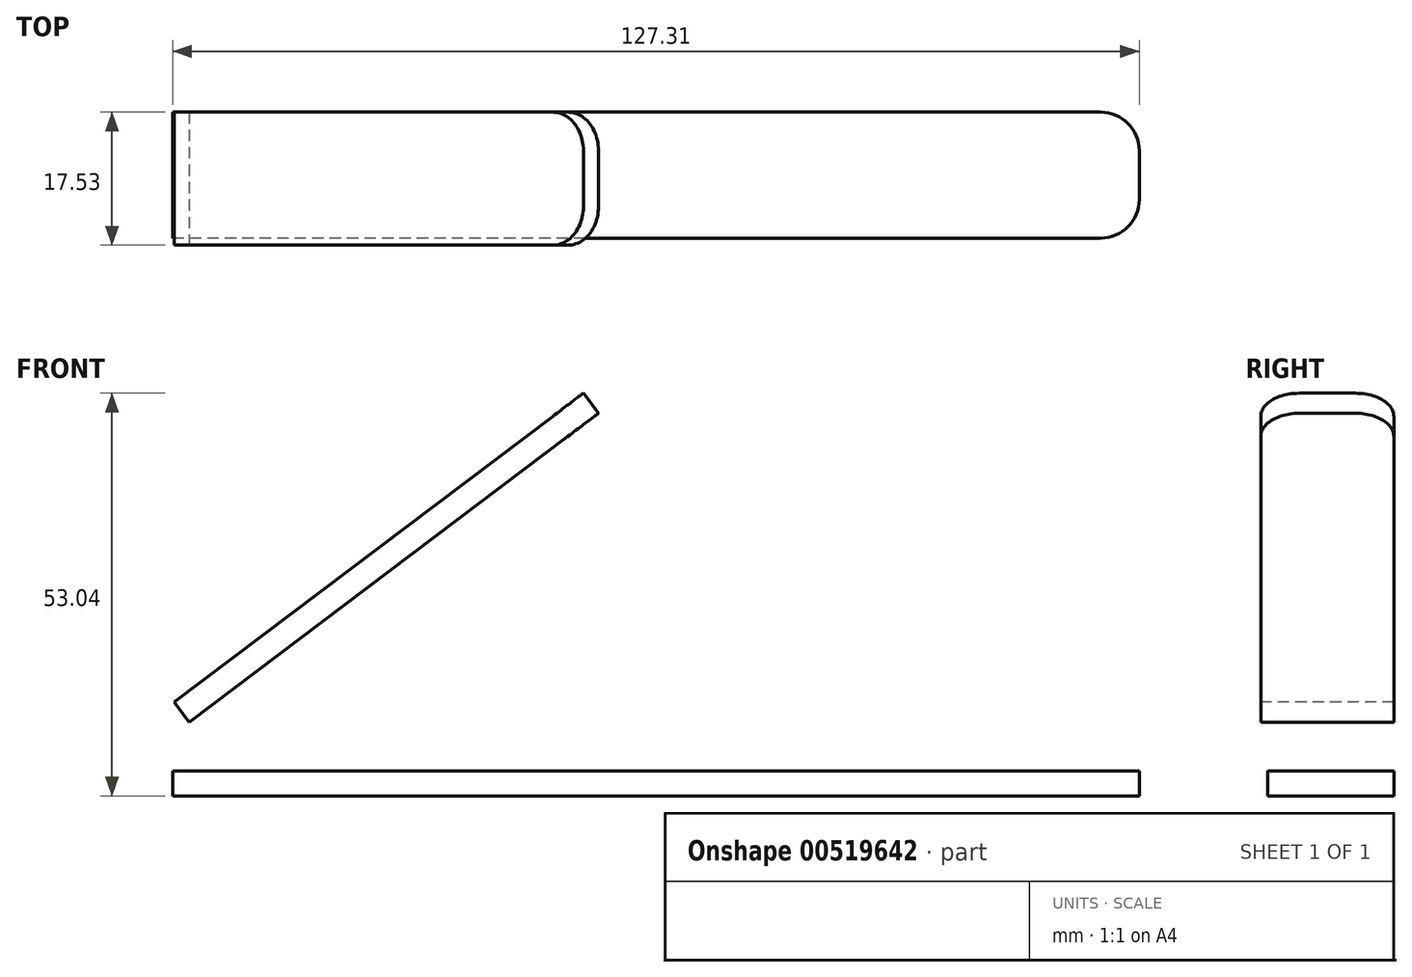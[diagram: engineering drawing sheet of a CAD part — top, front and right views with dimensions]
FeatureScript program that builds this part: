
annotation { "Feature Type Name" : "Feature", "Feature Type Description" : "" }
export const myFeature = defineFeature(function(context is Context, id is Id, definition is map)
    precondition{}
    {
        {
            var Q0;
            Q0=qCreatedBy(makeId("Front.planeOp"),FACE);
            var sketch = newSketch(context, id + "F0", { "sketchPlane" : qUnion([Q0])});
            skLineSegment(sketch, "E0", {"start": v(0, 0) * mm, "end": v(127, 0) * mm});
            skLineSegment(sketch, "E1", {"start": v(0, 12.2) * mm, "end": v(50.68, 50.46) * mm});
            skArc(sketch, "E2", {"start": v(0, 12.2) * mm, "mid": v(-3.04, 6.1) * mm, "end": v(0, 0) * mm});
            skSolve(sketch);
        }
        {
            var Q0;
            Q0=sQuery(id+"F0.wireOp",EDGE,"E1");
            cPlane(context, id + "F1", {"entities" : qUnion([Q0]), "cplaneType" : CPlaneType.LINE_ANGLE, "offset" : 25.4 * mm, "angle" : 90 * degree, "width" : 152.4 * mm, "height" : 152.4 * mm});
        }
        {
            var Q0;
            Q0=qCreatedBy(id+"F1.planeOp",FACE);
            var sketch = newSketch(context, id + "F2", { "sketchPlane" : qUnion([Q0])});
            skLineSegment(sketch, "E3.bottom", {"start": v(75.14, 0) * mm, "end": v(7.6, 0) * mm});
            skLineSegment(sketch, "E3.top", {"start": v(75.14, -17.53) * mm, "end": v(7.6, -17.53) * mm});
            skLineSegment(sketch, "E3.left", {"start": v(75.14, 0) * mm, "end": v(75.14, -17.53) * mm});
            skLineSegment(sketch, "E3.right", {"start": v(7.6, 0) * mm, "end": v(7.6, -17.53) * mm});
            skSolve(sketch);
        }
        {
            var Q0;
            Q0=qCreatedBy(makeId("Top.planeOp"),FACE);
            var sketch = newSketch(context, id + "F3", { "sketchPlane" : qUnion([Q0])});
            skLineSegment(sketch, "E4.bottom", {"start": v(127.31, 0) * mm, "end": v(0, 0) * mm});
            skLineSegment(sketch, "E4.top", {"start": v(127.31, -16.6) * mm, "end": v(0, -16.6) * mm});
            skLineSegment(sketch, "E4.left", {"start": v(127.31, 0) * mm, "end": v(127.31, -16.6) * mm});
            skLineSegment(sketch, "E4.right", {"start": v(0, 0.93) * mm, "end": v(0, -16.6) * mm});
            skSolve(sketch);
        }
        {
            var Q0;
            Q0=qCreatedBy(makeId("Front.planeOp"),FACE);
            cPlane(context, id + "F4", {"entities" : qUnion([Q0]), "cplaneType" : CPlaneType.OFFSET, "offset" : 17.53 * mm, "width" : 152.4 * mm, "height" : 152.4 * mm});
        }
        {
            var Q0;
            {var subQ0=sQuery(id+"F3.wireOp",EDGE,"E4.bottom");Q0=makeQuery(id+"F3.imprint","IMPRINT",FACE,{"disambiguationData":[TD([[makeQuery(id+"F3.imprint","IMPRINT",EDGE,{"derivedFrom":subQ0}),1.0]])]});}
            extrude(context, id + "F5", {"entities" : qUnion([Q0]), "depth" : 3.3 * mm, "offsetDistance" : 25.4 * mm});
        }
        {
            var Q0;
            Q0=makeQuery(id+"F2.imprint","IMPRINT",FACE,{"disambiguationData":[TD([[makeQuery(id+"F2.imprint","IMPRINT",EDGE,{"derivedFrom":sQuery(id+"F2.wireOp",EDGE,"E3.bottom")}),1.0]])]});
            extrude(context, id + "F6", {"entities" : qUnion([Q0]), "oppositeDirection" : true, "depth" : 3.3 * mm, "offsetDistance" : 25.4 * mm});
        }
        {
            var Q0;
            Q0=makeQuery(id+"F6.opExtrude","SWEPT_EDGE",EDGE,{"disambiguationData":[OSD([sQuery(id+"F2.wireOp",EDGE,"E3.bottom"),sQuery(id+"F2.wireOp",EDGE,"E3.left")])]});
            var Q1;
            Q1=makeQuery(id+"F6.opExtrude","SWEPT_EDGE",EDGE,{"disambiguationData":[OSD([sQuery(id+"F2.wireOp",EDGE,"E3.top"),sQuery(id+"F2.wireOp",EDGE,"E3.left")])]});
            var Q2;
            Q2=makeQuery(id+"F5.opExtrude","SWEPT_EDGE",EDGE,{"disambiguationData":[OSD([sQuery(id+"F3.wireOp",EDGE,"E4.bottom"),sQuery(id+"F3.wireOp",EDGE,"E4.left")])]});
            var Q3;
            Q3=makeQuery(id+"F5.opExtrude","SWEPT_EDGE",EDGE,{"disambiguationData":[OSD([sQuery(id+"F3.wireOp",EDGE,"E4.top"),sQuery(id+"F3.wireOp",EDGE,"E4.left")])]});
            fillet(context, id + "F7", {"entities" : qUnion([Q0, Q1, Q2, Q3]), "radius" : 5.08 * mm, "tangentPropagation" : true, "allowEdgeOverflow" : false});
        }
    });
